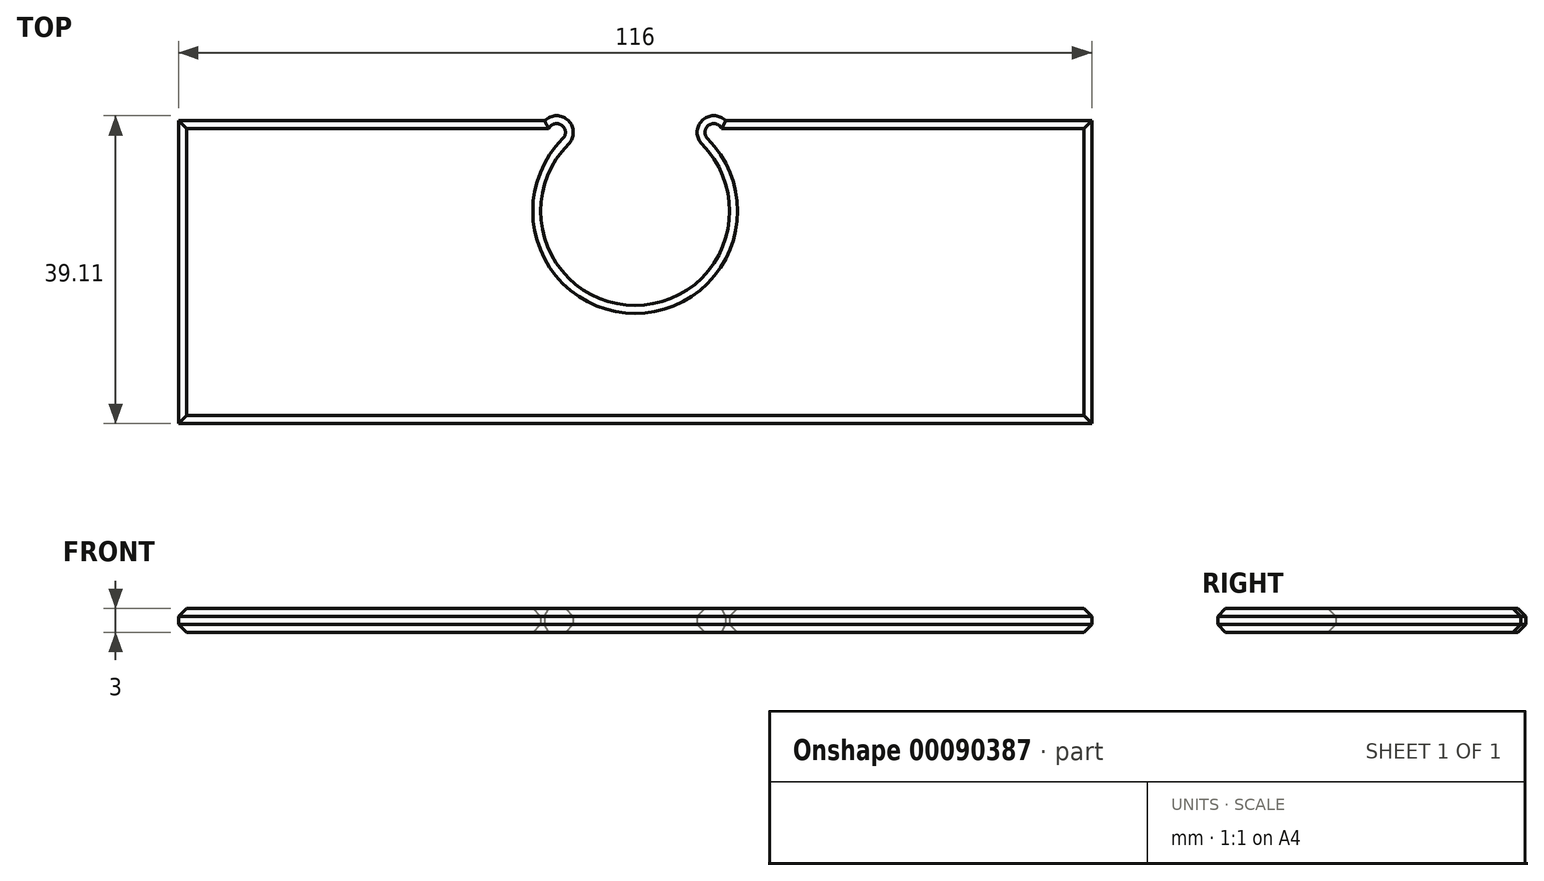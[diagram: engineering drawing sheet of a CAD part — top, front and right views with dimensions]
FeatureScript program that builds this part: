
annotation { "Feature Type Name" : "Feature", "Feature Type Description" : "" }
export const myFeature = defineFeature(function(context is Context, id is Id, definition is map)
    precondition{}
    {
        {
            var Q0;
            Q0=qCreatedBy(makeId("Top.planeOp"),FACE);
            var sketch = newSketch(context, id + "F0", { "sketchPlane" : qUnion([Q0])});
            skArc(sketch, "E0", {"start": v(-8.49, 8.49) * mm, "mid": v(0, -12) * mm, "end": v(8.49, 8.49) * mm});
            skCircle(sketch, "E1", {"center": v(0, 0) * mm, "radius": 32.5 * mm, "construction": true});
            skCircle(sketch, "E2.0", {"center": v(0, 0) * mm, "radius": 37.5 * mm, "construction": true});
            skLineSegment(sketch, "E3", {"start": v(0, 33.53) * mm, "end": v(0, -37.5) * mm, "construction": true});
            skLineSegment(sketch, "E4", {"start": v(-37.5, 0) * mm, "end": v(37.5, 0) * mm, "construction": true});
            skLineSegment(sketch, "E5", {"start": v(0, 0) * mm, "end": v(26.52, 26.52) * mm, "construction": true});
            skLineSegment(sketch, "E6", {"start": v(-58, -27) * mm, "end": v(58, -27) * mm});
            skPoint(sketch, "E7", {"position": v(0, -12) * mm});
            skPoint(sketch, "E8", {"position": v(12, 0) * mm});
            skLineSegment(sketch, "E9", {"start": v(58, -27) * mm, "end": v(58, 11.49) * mm});
            skLineSegment(sketch, "E10", {"start": v(58, 11.49) * mm, "end": v(11.49, 11.49) * mm});
            skLineSegment(sketch, "E11", {"start": v(-58, -27) * mm, "end": v(-58, 11.49) * mm});
            skLineSegment(sketch, "E12", {"start": v(-58, 11.49) * mm, "end": v(-11.49, 11.49) * mm});
            skArc(sketch, "E13", {"start": v(8.49, 8.49) * mm, "mid": v(8.49, 11.49) * mm, "end": v(11.49, 11.49) * mm});
            skArc(sketch, "E14", {"start": v(-8.49, 8.49) * mm, "mid": v(-8.49, 11.49) * mm, "end": v(-11.49, 11.49) * mm});
            skSolve(sketch);
        }
        {
            var Q0;
            Q0 = qSketchRegion(id + "F0", true);
            extrude(context, id + "F1", {"entities" : qUnion([Q0]), "endBound" : BoundingType.SYMMETRIC, "depth" : 3 * mm});
        }
        {
            var Q0;
            Q0=makeQuery(id+"F1.opExtrude","CAP_EDGE",EDGE,{"disambiguationData":[OSD([sQuery(id+"F0.wireOp",EDGE,"E0")])],"isStart":false});
            var Q1;
            Q1=makeQuery(id+"F1.opExtrude","CAP_EDGE",EDGE,{"disambiguationData":[OSD([sQuery(id+"F0.wireOp",EDGE,"E13")])],"isStart":false});
            var Q2;
            Q2=makeQuery(id+"F1.opExtrude","CAP_EDGE",EDGE,{"disambiguationData":[OSD([sQuery(id+"F0.wireOp",EDGE,"E10")])],"isStart":false});
            var Q3;
            Q3=makeQuery(id+"F1.opExtrude","CAP_EDGE",EDGE,{"disambiguationData":[OSD([sQuery(id+"F0.wireOp",EDGE,"E9")])],"isStart":false});
            var Q4;
            Q4=makeQuery(id+"F1.opExtrude","CAP_EDGE",EDGE,{"disambiguationData":[OSD([sQuery(id+"F0.wireOp",EDGE,"E6")])],"isStart":false});
            var Q5;
            Q5=makeQuery(id+"F1.opExtrude","CAP_EDGE",EDGE,{"disambiguationData":[OSD([sQuery(id+"F0.wireOp",EDGE,"E11")])],"isStart":false});
            var Q6;
            Q6=makeQuery(id+"F1.opExtrude","CAP_EDGE",EDGE,{"disambiguationData":[OSD([sQuery(id+"F0.wireOp",EDGE,"E12")])],"isStart":false});
            var Q7;
            Q7=makeQuery(id+"F1.opExtrude","CAP_EDGE",EDGE,{"disambiguationData":[OSD([sQuery(id+"F0.wireOp",EDGE,"E14")])],"isStart":false});
            var Q8;
            Q8=makeQuery(id+"F1.opExtrude","CAP_FACE",FACE,{"disambiguationData":[OSD([sQuery(id+"F0.wireOp",EDGE,"E0"),sQuery(id+"F0.wireOp",EDGE,"E6"),sQuery(id+"F0.wireOp",EDGE,"E9"),sQuery(id+"F0.wireOp",EDGE,"E10"),sQuery(id+"F0.wireOp",EDGE,"E11"),sQuery(id+"F0.wireOp",EDGE,"E12"),sQuery(id+"F0.wireOp",EDGE,"E13"),sQuery(id+"F0.wireOp",EDGE,"E14")])],"isStart":false});
            var Q9;
            Q9=makeQuery(id+"F1.opExtrude","CAP_EDGE",EDGE,{"disambiguationData":[OSD([sQuery(id+"F0.wireOp",EDGE,"E12")])],"isStart":true});
            var Q10;
            Q10=makeQuery(id+"F1.opExtrude","CAP_EDGE",EDGE,{"disambiguationData":[OSD([sQuery(id+"F0.wireOp",EDGE,"E11")])],"isStart":true});
            var Q11;
            Q11=makeQuery(id+"F1.opExtrude","CAP_EDGE",EDGE,{"disambiguationData":[OSD([sQuery(id+"F0.wireOp",EDGE,"E6")])],"isStart":true});
            var Q12;
            Q12=makeQuery(id+"F1.opExtrude","CAP_EDGE",EDGE,{"disambiguationData":[OSD([sQuery(id+"F0.wireOp",EDGE,"E0")])],"isStart":true});
            var Q13;
            Q13=makeQuery(id+"F1.opExtrude","CAP_EDGE",EDGE,{"disambiguationData":[OSD([sQuery(id+"F0.wireOp",EDGE,"E14")])],"isStart":true});
            var Q14;
            Q14=makeQuery(id+"F1.opExtrude","CAP_EDGE",EDGE,{"disambiguationData":[OSD([sQuery(id+"F0.wireOp",EDGE,"E9")])],"isStart":true});
            var Q15;
            Q15=makeQuery(id+"F1.opExtrude","CAP_EDGE",EDGE,{"disambiguationData":[OSD([sQuery(id+"F0.wireOp",EDGE,"E10")])],"isStart":true});
            var Q16;
            Q16=makeQuery(id+"F1.opExtrude","CAP_EDGE",EDGE,{"disambiguationData":[OSD([sQuery(id+"F0.wireOp",EDGE,"E13")])],"isStart":true});
            chamfer(context, id + "F2", {"entities" : qUnion([Q0, Q1, Q2, Q3, Q4, Q5, Q6, Q7, Q8, Q9, Q10, Q11, Q12, Q13, Q14, Q15, Q16]), "width" : 1 * mm, "tangentPropagation" : true});
        }
    });
